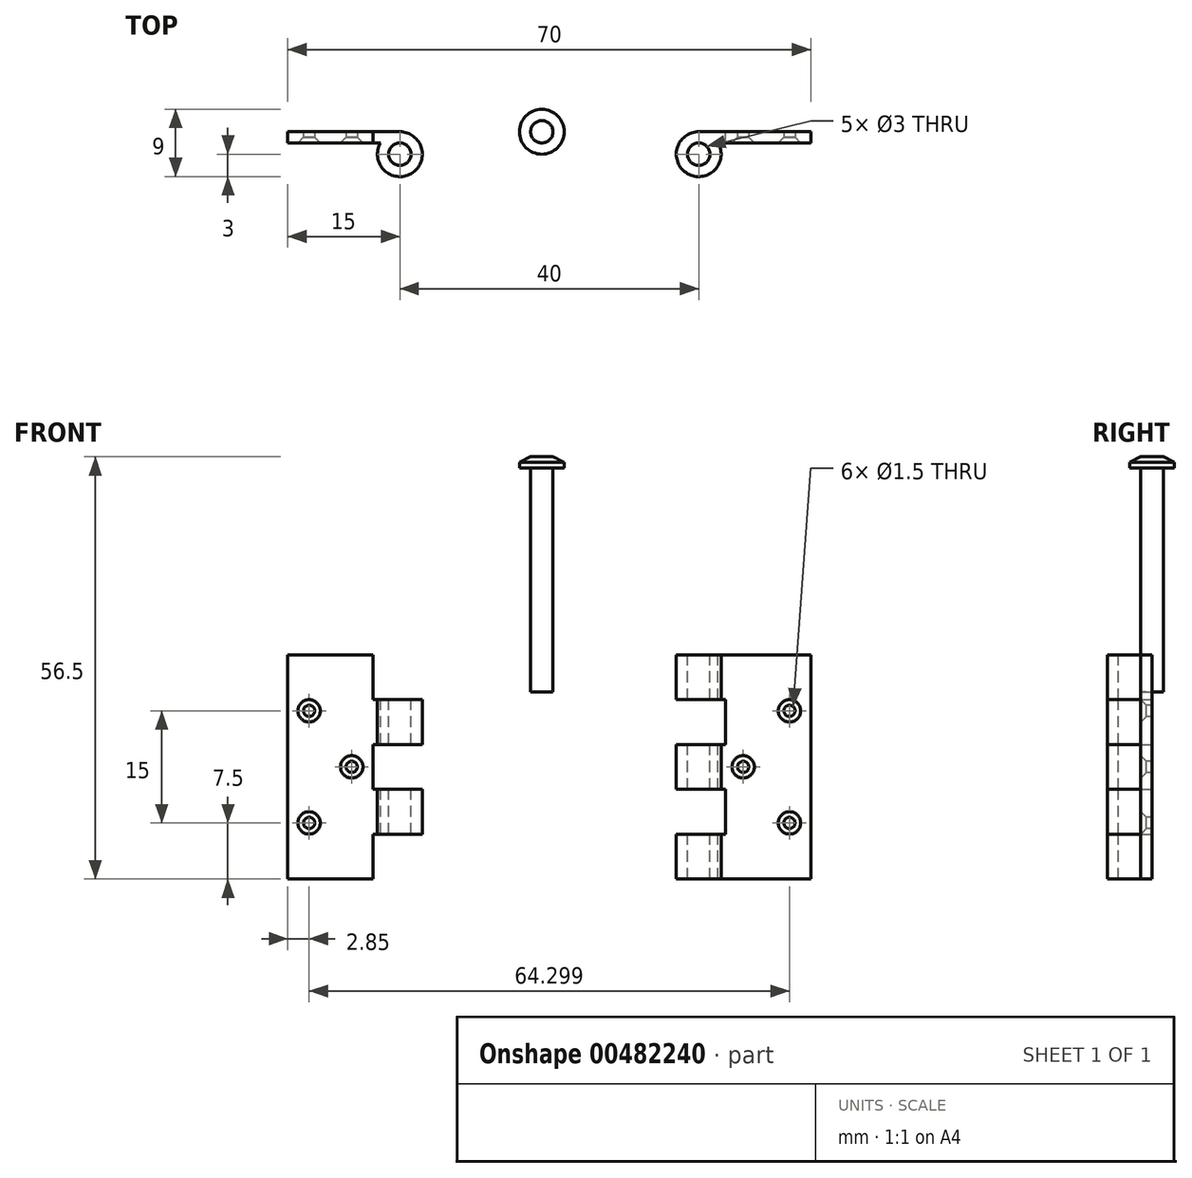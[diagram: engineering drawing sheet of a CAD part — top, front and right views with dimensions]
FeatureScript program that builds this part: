
annotation { "Feature Type Name" : "Feature", "Feature Type Description" : "" }
export const myFeature = defineFeature(function(context is Context, id is Id, definition is map)
    precondition{}
    {
        {
            var Q0;
            Q0=qCreatedBy(makeId("Front.planeOp"),FACE);
            var sketch = newSketch(context, id + "F0", { "sketchPlane" : qUnion([Q0])});
            skLineSegment(sketch, "E0.bottom", {"start": v(-35, -15) * mm, "end": v(-20, -15) * mm});
            skLineSegment(sketch, "E0.top", {"start": v(-35, 15) * mm, "end": v(-20, 15) * mm});
            skLineSegment(sketch, "E0.left", {"start": v(-35, -15) * mm, "end": v(-35, 15) * mm});
            skLineSegment(sketch, "E0.right", {"start": v(-20, -15) * mm, "end": v(-20, 15) * mm});
            skLineSegment(sketch, "E1.bottom", {"start": v(20, -15) * mm, "end": v(35, -15) * mm});
            skLineSegment(sketch, "E1.top", {"start": v(20, 15) * mm, "end": v(35, 15) * mm});
            skLineSegment(sketch, "E1.left", {"start": v(20, -15) * mm, "end": v(20, 15) * mm});
            skLineSegment(sketch, "E1.right", {"start": v(35, -15) * mm, "end": v(35, 15) * mm});
            skSolve(sketch);
        }
        {
            var Q0;
            Q0 = qSketchRegion(id + "F0", true);
            extrude(context, id + "F1", {"entities" : qUnion([Q0]), "depth" : 1.5 * mm});
        }
        {
            var Q0;
            Q0=makeQuery(id+"F1.opExtrude","SWEPT_FACE",FACE,{"disambiguationData":[OSD([sQuery(id+"F0.wireOp",EDGE,"E0.top")])]});
            var sketch = newSketch(context, id + "F2", { "sketchPlane" : qUnion([Q0])});
            skCircle(sketch, "E2", {"center": v(-20, -3) * mm, "radius": 1.5 * mm});
            skPoint(sketch, "E2.centerSnap0", {"position": v(-20, -0.75) * mm});
            skCircle(sketch, "E3", {"center": v(-20, -3) * mm, "radius": 3 * mm});
            skSolve(sketch);
        }
        {
            var Q0;
            {var subQ0=sQuery(id+"F2.wireOp",EDGE,"E2");Q0=makeQuery(id+"F2.imprint","IMPRINT",FACE,{"disambiguationData":[TD([[makeQuery(id+"F2.imprint","IMPRINT",EDGE,{"derivedFrom":subQ0}),-1.0]])]});}
            var Q1;
            {var subQ1=sQuery(id+"F0.wireOp",EDGE,"E0.top");var subQ2=makeQuery(id+"F1.opExtrude","SWEPT_EDGE",EDGE,{"disambiguationData":[OSD([subQ1,sQuery(id+"F0.wireOp",EDGE,"E0.right")])]});Q1=makeQuery(id+"F2.imprint","IMPRINT",FACE,{"disambiguationData":[TD([[makeQuery(id+"F2.imprint","IMPRINT",EDGE,{"derivedFrom":subQ2}),1.0]])]});}
            var Q2;
            Q2=sQuery(id+"F2.wireOp",EDGE,"E3");
            var Q3;
            Q3=sQuery(id+"F2.wireOp",EDGE,"E2");
            var Q4;
            Q4=makeQuery(id+"F1.opExtrude","SWEPT_FACE",FACE,{"disambiguationData":[OSD([sQuery(id+"F0.wireOp",EDGE,"E0.bottom")])]});
            extrude(context, id + "F3", {"entities" : qUnion([Q0, Q1]), "operationType" : NewBodyOperationType.ADD, "surfaceEntities" : qUnion([Q2, Q3]), "endBound" : BoundingType.UP_TO_SURFACE, "oppositeDirection" : true, "endBoundEntityFace" : qUnion([Q4]), "depth" : 30 * mm});
        }
        {
            var Q0;
            Q0=makeQuery(id+"F1.opExtrude","SWEPT_FACE",FACE,{"disambiguationData":[OSD([sQuery(id+"F0.wireOp",EDGE,"E1.top")])]});
            var sketch = newSketch(context, id + "F4", { "sketchPlane" : qUnion([Q0])});
            skCircle(sketch, "E4", {"center": v(20, -3) * mm, "radius": 1.5 * mm});
            skPoint(sketch, "E4.centerSnap0", {"position": v(20, -0.75) * mm});
            skCircle(sketch, "E5", {"center": v(20, -3) * mm, "radius": 3 * mm});
            skSolve(sketch);
        }
        {
            var Q0;
            Q0 = qSketchRegion(id + "F4", true);
            var Q1;
            Q1=makeQuery(id+"F1.opExtrude","SWEPT_FACE",FACE,{"disambiguationData":[OSD([sQuery(id+"F0.wireOp",EDGE,"E1.bottom")])]});
            extrude(context, id + "F5", {"entities" : qUnion([Q0]), "operationType" : NewBodyOperationType.ADD, "endBound" : BoundingType.UP_TO_SURFACE, "oppositeDirection" : true, "endBoundEntityFace" : qUnion([Q1]), "depth" : 25 * mm});
        }
        {
            var Q0;
            Q0=qCreatedBy(makeId("Front.planeOp"),FACE);
            var sketch = newSketch(context, id + "F6", { "sketchPlane" : qUnion([Q0])});
            skLineSegment(sketch, "E6.bottom", {"start": v(-23.6, -15) * mm, "end": v(23.6, -15) * mm});
            skLineSegment(sketch, "E6.top", {"start": v(-23.6, 15) * mm, "end": v(23.6, 15) * mm});
            skLineSegment(sketch, "E6.left", {"start": v(-23.6, -15) * mm, "end": v(-23.6, 15) * mm});
            skLineSegment(sketch, "E6.right", {"start": v(23.6, -15) * mm, "end": v(23.6, 15) * mm});
            skLineSegment(sketch, "E7", {"start": v(0, 15) * mm, "end": v(0, -15) * mm});
            skLineSegment(sketch, "E8", {"start": v(-23.6, 9) * mm, "end": v(23.6, 9) * mm});
            skLineSegment(sketch, "E9", {"start": v(-23.6, -9) * mm, "end": v(23.6, -9) * mm});
            skLineSegment(sketch, "E10", {"start": v(-23.6, 3) * mm, "end": v(23.6, 3) * mm});
            skLineSegment(sketch, "E11", {"start": v(-23.6, -3) * mm, "end": v(23.6, -3) * mm});
            skLineSegment(sketch, "E12", {"start": v(-16.6, 15) * mm, "end": v(-16.6, -15) * mm});
            skLineSegment(sketch, "E13", {"start": v(16.6, 15) * mm, "end": v(16.6, -15) * mm});
            skSolve(sketch);
        }
        {
            var Q0;
            {var subQ0=sQuery(id+"F6.wireOp",EDGE,"E6.left");var subQ1=sQuery(id+"F6.wireOp",EDGE,"E6.top");var subQ2=makeQuery(id+"F6.imprint","INTERSECT",VERTEX,{"derivedFrom":[subQ1,subQ0]});Q0=makeQuery(id+"F6.imprint","IMPRINT",FACE,{"disambiguationData":[TD([[makeQuery(id+"F6.imprint","IMPRINT",EDGE,{"disambiguationData":[TD([[subQ2,-1.0]])],"derivedFrom":subQ1}),-1.0]])]});}
            var Q1;
            {var subQ0=sQuery(id+"F6.wireOp",EDGE,"E8");var subQ1=sQuery(id+"F6.wireOp",EDGE,"E6.right");var subQ2=makeQuery(id+"F6.imprint","INTERSECT",VERTEX,{"derivedFrom":[subQ1,subQ0]});Q1=makeQuery(id+"F6.imprint","IMPRINT",FACE,{"disambiguationData":[TD([[makeQuery(id+"F6.imprint","IMPRINT",EDGE,{"disambiguationData":[TD([[subQ2,1.0]])],"derivedFrom":subQ1}),1.0]])]});}
            var Q2;
            {var subQ0=sQuery(id+"F6.wireOp",EDGE,"E10");var subQ1=sQuery(id+"F6.wireOp",EDGE,"E6.left");var subQ2=makeQuery(id+"F6.imprint","INTERSECT",VERTEX,{"derivedFrom":[subQ1,subQ0]});Q2=makeQuery(id+"F6.imprint","IMPRINT",FACE,{"disambiguationData":[TD([[makeQuery(id+"F6.imprint","IMPRINT",EDGE,{"disambiguationData":[TD([[subQ2,1.0]])],"derivedFrom":subQ1}),-1.0]])]});}
            var Q3;
            {var subQ0=sQuery(id+"F6.wireOp",EDGE,"E9");var subQ1=sQuery(id+"F6.wireOp",EDGE,"E6.right");var subQ2=makeQuery(id+"F6.imprint","INTERSECT",VERTEX,{"derivedFrom":[subQ1,subQ0]});Q3=makeQuery(id+"F6.imprint","IMPRINT",FACE,{"disambiguationData":[TD([[makeQuery(id+"F6.imprint","IMPRINT",EDGE,{"disambiguationData":[TD([[subQ2,-1.0]])],"derivedFrom":subQ1}),1.0]])]});}
            var Q4;
            {var subQ0=sQuery(id+"F6.wireOp",EDGE,"E6.left");var subQ1=sQuery(id+"F6.wireOp",EDGE,"E6.bottom");var subQ2=makeQuery(id+"F6.imprint","INTERSECT",VERTEX,{"derivedFrom":[subQ1,subQ0]});Q4=makeQuery(id+"F6.imprint","IMPRINT",FACE,{"disambiguationData":[TD([[makeQuery(id+"F6.imprint","IMPRINT",EDGE,{"disambiguationData":[TD([[subQ2,-1.0]])],"derivedFrom":subQ1}),1.0]])]});}
            extrude(context, id + "F7", {"entities" : qUnion([Q0, Q1, Q2, Q3, Q4]), "operationType" : NewBodyOperationType.REMOVE, "depth" : 25 * mm});
        }
        {
            var Q0;
            Q0=qCreatedBy(makeId("Front.planeOp"),FACE);
            var sketch = newSketch(context, id + "F8", { "sketchPlane" : qUnion([Q0])});
            skLineSegment(sketch, "E14", {"start": v(-2.5, 41.5) * mm, "end": v(-1, 41.5) * mm});
            skLineSegment(sketch, "E15", {"start": v(-1, 41.5) * mm, "end": v(-1, 10) * mm});
            skLineSegment(sketch, "E16", {"start": v(-1, 10) * mm, "end": v(-2.5, 10) * mm});
            skLineSegment(sketch, "E17", {"start": v(-2.5, 10) * mm, "end": v(-2.5, 40) * mm});
            skLineSegment(sketch, "E18", {"start": v(-2.5, 40) * mm, "end": v(-4, 40) * mm});
            skLineSegment(sketch, "E19", {"start": v(-4, 40.75) * mm, "end": v(-2.5, 41.5) * mm});
            skLineSegment(sketch, "E20", {"start": v(-4, 40) * mm, "end": v(-4, 40.75) * mm});
            skSolve(sketch);
        }
        {
            var Q0;
            Q0=makeQuery(id+"F8.imprint","IMPRINT",FACE,{"disambiguationData":[TD([[makeQuery(id+"F8.imprint","IMPRINT",EDGE,{"derivedFrom":sQuery(id+"F8.wireOp",EDGE,"E14")}),-1.0]])]});
            var Q1;
            Q1=sQuery(id+"F8.wireOp",EDGE,"E15");
            revolve(context, id + "F9", {"entities" : qUnion([Q0]), "axis" : qUnion([Q1]), "revolveType" : RevolveType.FULL});
        }
        {
            var Q0;
            Q0=makeQuery(id+"F1.opExtrude","CAP_FACE",FACE,{"disambiguationData":[OSD([sQuery(id+"F0.wireOp",EDGE,"E0.bottom"),sQuery(id+"F0.wireOp",EDGE,"E0.top"),sQuery(id+"F0.wireOp",EDGE,"E0.left"),sQuery(id+"F0.wireOp",EDGE,"E0.right")])],"isStart":false});
            var sketch = newSketch(context, id + "F10", { "sketchPlane" : qUnion([Q0])});
            skLineSegment(sketch, "E21", {"start": v(-29.3, 15) * mm, "end": v(-29.3, -15) * mm, "construction": true});
            skLineSegment(sketch, "E22", {"start": v(-35, 0) * mm, "end": v(-23.6, 0) * mm, "construction": true});
            skLineSegment(sketch, "E23", {"start": v(-35, 7.5) * mm, "end": v(-23.6, 7.5) * mm, "construction": true});
            skLineSegment(sketch, "E24", {"start": v(-35, -7.5) * mm, "end": v(-23.6, -7.5) * mm, "construction": true});
            skLineSegment(sketch, "E25", {"start": v(-32.15, 15) * mm, "end": v(-32.15, -15) * mm, "construction": true});
            skLineSegment(sketch, "E26", {"start": v(-26.45, 15) * mm, "end": v(-26.45, -15) * mm, "construction": true});
            skPoint(sketch, "E27", {"position": v(-32.15, 7.5) * mm});
            skPoint(sketch, "E28", {"position": v(-26.45, 0) * mm});
            skPoint(sketch, "E29", {"position": v(-32.15, -7.5) * mm});
            skSolve(sketch);
        }
        {
            var Q0;
            Q0=makeQuery(id+"F1.opExtrude","CAP_FACE",FACE,{"disambiguationData":[OSD([sQuery(id+"F0.wireOp",EDGE,"E1.bottom"),sQuery(id+"F0.wireOp",EDGE,"E1.top"),sQuery(id+"F0.wireOp",EDGE,"E1.left"),sQuery(id+"F0.wireOp",EDGE,"E1.right")])],"isStart":false});
            var sketch = newSketch(context, id + "F11", { "sketchPlane" : qUnion([Q0])});
            skLineSegment(sketch, "E30", {"start": v(35, 0) * mm, "end": v(23.6, 0) * mm, "construction": true});
            skPoint(sketch, "E30.endSnap0", {"position": v(22.6, 0) * mm});
            skLineSegment(sketch, "E31", {"start": v(23.6, -7.5) * mm, "end": v(35, -7.5) * mm, "construction": true});
            skLineSegment(sketch, "E32", {"start": v(23.6, 7.5) * mm, "end": v(35, 7.5) * mm, "construction": true});
            skLineSegment(sketch, "E33", {"start": v(28.8, 15) * mm, "end": v(28.8, -15) * mm, "construction": true});
            skLineSegment(sketch, "E34", {"start": v(32.15, 15) * mm, "end": v(32.15, -15) * mm, "construction": true});
            skLineSegment(sketch, "E35", {"start": v(25.95, 15) * mm, "end": v(25.95, -15) * mm, "construction": true});
            skPoint(sketch, "E36", {"position": v(32.15, 7.5) * mm});
            skPoint(sketch, "E37", {"position": v(25.95, 0) * mm});
            skPoint(sketch, "E38", {"position": v(32.15, -7.5) * mm});
            skSolve(sketch);
        }
        {
            var Q0;
            Q0=sQuery(id+"F10.wireOp",VERTEX,"E27");
            var Q1;
            Q1=sQuery(id+"F10.wireOp",VERTEX,"E28");
            var Q2;
            Q2=sQuery(id+"F10.wireOp",VERTEX,"E29");
            var Q3;
            Q3=sQuery(id+"F11.wireOp",VERTEX,"E38");
            var Q4;
            Q4=sQuery(id+"F11.wireOp",VERTEX,"E37");
            var Q5;
            Q5=sQuery(id+"F11.wireOp",VERTEX,"E36");
            var Q6;
            Q6=makeQuery(id+"F1.opExtrude","SWEPT_BODY",BODY,{"disambiguationData":[OSD([sQuery(id+"F0.wireOp",EDGE,"E0.bottom"),sQuery(id+"F0.wireOp",EDGE,"E0.top"),sQuery(id+"F0.wireOp",EDGE,"E0.left"),sQuery(id+"F0.wireOp",EDGE,"E0.right")])]});
            var Q7;
            Q7=makeQuery(id+"F1.opExtrude","SWEPT_BODY",BODY,{"disambiguationData":[OSD([sQuery(id+"F0.wireOp",EDGE,"E1.bottom"),sQuery(id+"F0.wireOp",EDGE,"E1.top"),sQuery(id+"F0.wireOp",EDGE,"E1.left"),sQuery(id+"F0.wireOp",EDGE,"E1.right")])]});
            hole(context, id + "F12", {"style" : HoleStyle.C_SINK, "endStyle" : HoleEndStyle.THROUGH, "holeDiameter" : 1.5 * mm, "cSinkDiameter" : 3 * mm, "cSinkAngle" : 90 * degree, "tappedDepth" : 12 * mm, "tapClearance" : 3, "locations" : qUnion([Q0, Q1, Q2, Q3, Q4, Q5]), "scope" : qUnion([Q6, Q7])});
        }
    });
